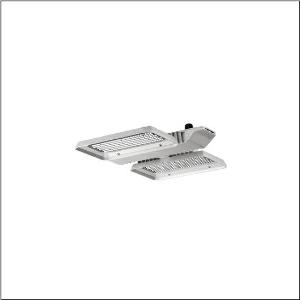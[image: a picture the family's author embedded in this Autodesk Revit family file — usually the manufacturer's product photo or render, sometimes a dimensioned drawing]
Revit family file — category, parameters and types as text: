
# Revit family: highbay_11_51hla2d14fca
name_source: partatom
category: Lighting Fixtures
units: mm (PartAtom-declared; Revit-internal decimal feet)

## family parameters
Cut with Voids When Loaded = No
Host = Face
Light Source = No
Part Type = Normal
Room Calculation Point = No
Round Connector Dimension = Use Diameter
Shared = No

## types (1)
- --- (1 x LED, 14400 lm, 81.2 W, 4000K)
    Apparent Load = 81 VA
    CIE Flux Codes = 89 96 99 100 100
    Color Rendering = 80
    Color Temperature = 4000K
    Default Elevation = 1800 mm
    Description = Highbay 11, LED high bay luminaire, primary light control with lens, of PMMA, light emission: direct distribution, primary light characteristic: symmetric, installation type: surface-mounted, suspended mounting, for 1x 2x LED, rated luminous flux: 14.400lm, luminous efficacy: 177lm/W, light colour: 840, colour temperature: 4000K, control gear: DALI, with terminal, 5-pole, max. 2.5mm², mains connection: 230..240V, AC, 50/60Hz, rated input power: 81W, LED unit, of diecast aluminium, unplated, bead blasted, silver, length: 470mm, width: 500mm, height: 65mm, housing, of diecast aluminium, uncoated, bead blasted, silver, protection rating (complete): IP65, insulation class (complete): insulation class I (protective earthing), certification: CE, ENEC, VDE, UKCA, protection symbol: D, impact resistance: IK08 with glass or PC cover, permissible operating ambient temperature: -35..+55°C, reducing of maximum allowable ambient temperature of 5°C with ceiling mounting, corresponds to IFS (International Featured Standards) requirements for safety and quality in the food industry, packaging unit: 1 piece
    Height = 95 mm
    Lamp = 1 x LED
    Lamp Light Flux = 14400 lm
    Lamp Power = 81.2 W
    Lamp count = 1
    Length = 468 mm
    Luminous efficacy = 177 lm/W
    Manufacturer = Siteco
    ModVariant = No
    Model = 51HLA2D14FCA
    Mounting Place = Ceiling
    Mounting Type = Pendant
    Number of Poles = 1
    OnlyDefault = Yes
    Power Factor = 1
    Product Name = Highbay 11
    Product group = LED high bay luminaire
    ProductGroupID = 903
    Protection Class = Protection class I
    Protection Degree = IP 65
    RLX_Detail_Level = 1
    RLX_Emergency_Light_Flux = 0 lm
    RLX_Emergency_Type = 0
    RLX_Emergency_Type_DB = No
    RlxData = <blob elided: 86249 chars, md5=abf22f88>
    Socket = socket
    Standby Power = 0 W
    System Light Flux = 14400 lm
    System Power = 81 W
    Type Comments = factory setting: luminous flux: 100 % | dim-lin: 254 | 460 mA
    Type Image = l_1003425.jpg
    URL = http://relux.com
    VarID = @adj_201430
    Voltage = 0 V
    Weight = 0.00 kg
    Width = 501 mm

## geometry (parser evidence)
native form markers: Blend x4, Sweep x14
no freeform markers — native parametric forms only
